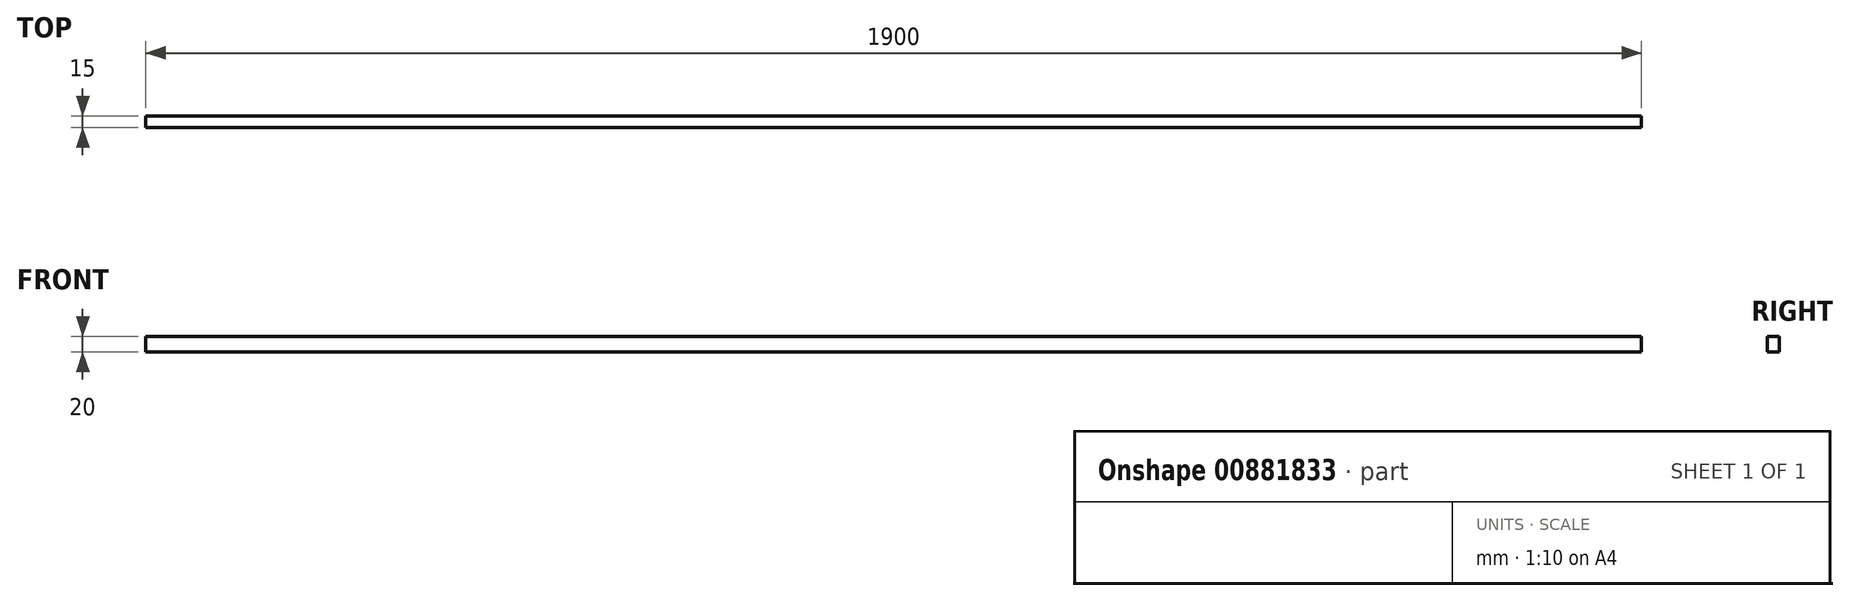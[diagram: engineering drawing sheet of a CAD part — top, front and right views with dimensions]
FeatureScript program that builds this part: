
annotation { "Feature Type Name" : "Feature", "Feature Type Description" : "" }
export const myFeature = defineFeature(function(context is Context, id is Id, definition is map)
    precondition{}
    {
        {
            var Q0;
            Q0=qCreatedBy(makeId("Front.planeOp"),FACE);
            var sketch = newSketch(context, id + "F0", { "sketchPlane" : qUnion([Q0])});
            skLineSegment(sketch, "E0", {"start": v(-48.8, 25.89) * mm, "end": v(1851.2, 25.89) * mm});
            skLineSegment(sketch, "E1", {"start": v(1851.2, 45.89) * mm, "end": v(-48.8, 45.89) * mm});
            skLineSegment(sketch, "E2", {"start": v(-48.8, 45.89) * mm, "end": v(-48.8, 25.89) * mm});
            skLineSegment(sketch, "E3", {"start": v(1851.2, 25.89) * mm, "end": v(1851.2, 45.89) * mm});
            skSolve(sketch);
        }
        {
            var Q0;
            Q0=qSketchRegion(id+"F0",true);
            extrude(context, id + "F1", {"entities" : qUnion([Q0]), "depth" : 15 * mm, "offsetDistance" : 25 * mm});
        }
    });
